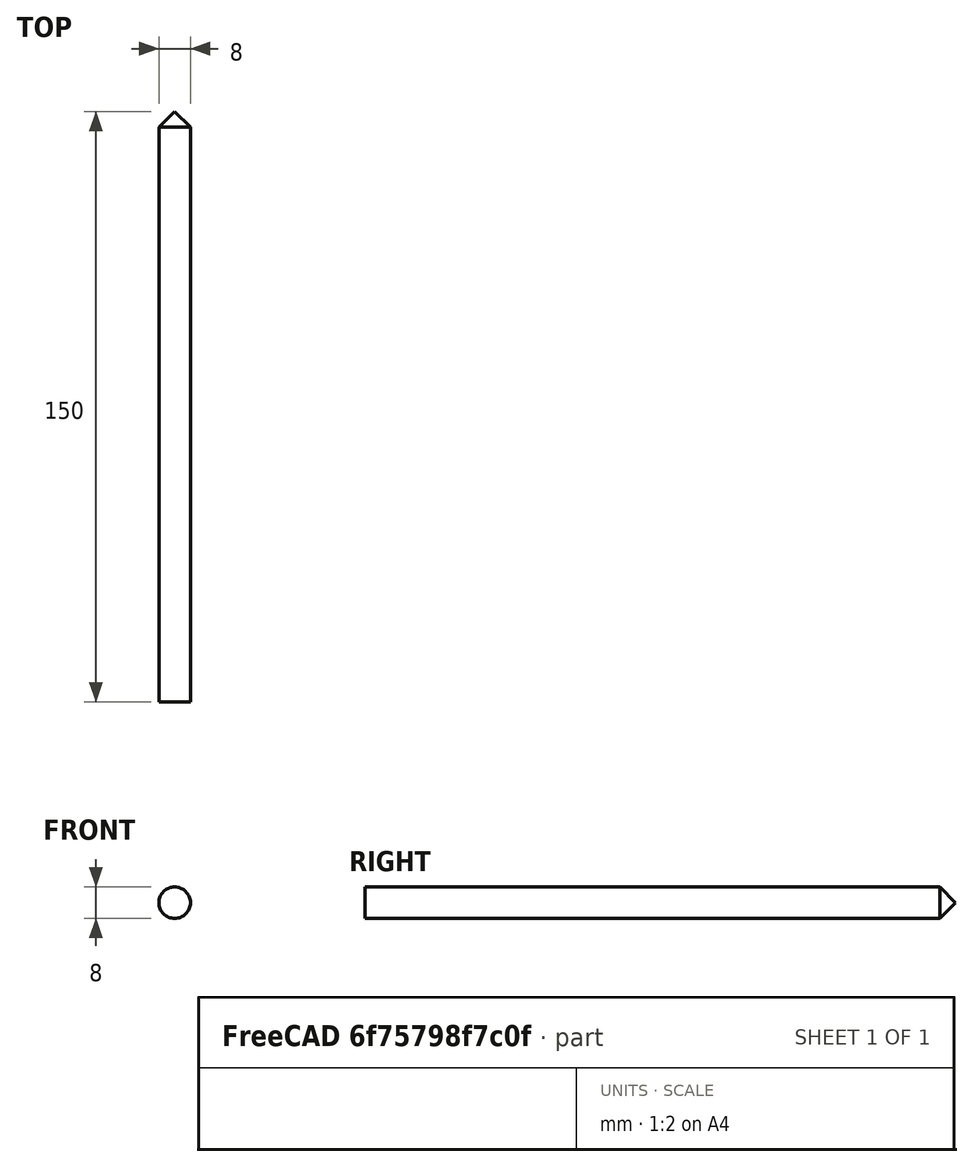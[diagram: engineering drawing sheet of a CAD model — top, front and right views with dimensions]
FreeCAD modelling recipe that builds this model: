
FCSTD DOCUMENT  (FreeCAD 0.18.3R)
Label: pen
License: All rights reserved
LicenseURL: http://en.wikipedia.org/wiki/All_rights_reserved
objects: Sketcher::SketchObject×1, PartDesign::Pad×1, PartDesign::Chamfer×1, PartDesign::Body×1
note: 5 computed .brp shape members not serialized (recipe doc carries the construction recipe); baked Part::Feature solids carry a one-line shape summary decoded from their .brp

FEATURE [Sketcher::SketchObject] Sketch
  MapMode = 5
  Placement = pos=(0,0,0) rot=(1,0,0;1.5708rad)
  Support = -> [XZ_Plane]
  sketch-geometry (1):
    g0: Circle CenterX=0 CenterY=0 CenterZ=0 NormalX=0 NormalY=0 NormalZ=1 AngleXU=0 Radius=4
  constraints (2):
    c: Coincident(g0,g-1)
    c: Radius(g0) = 4
FEATURE [PartDesign::Pad] Pad
  Length = 150
  Length2 = 100
  Placement = pos=(0,0,0) rot=(1,0,0;1.5708rad)
  Profile = -> Sketch
  Type = 0
FEATURE [PartDesign::Chamfer] Chamfer
  Base = -> Pad [Edge2]
  BaseFeature = -> Pad
  Placement = pos=(0,0,0) rot=(1,0,0;1.5708rad)
  Size = 4
FEATURE [PartDesign::Body] Body  label="pen"
  Group = -> [Sketch,Pad,Chamfer]
  Origin = -> Origin
  Tip = -> Chamfer
